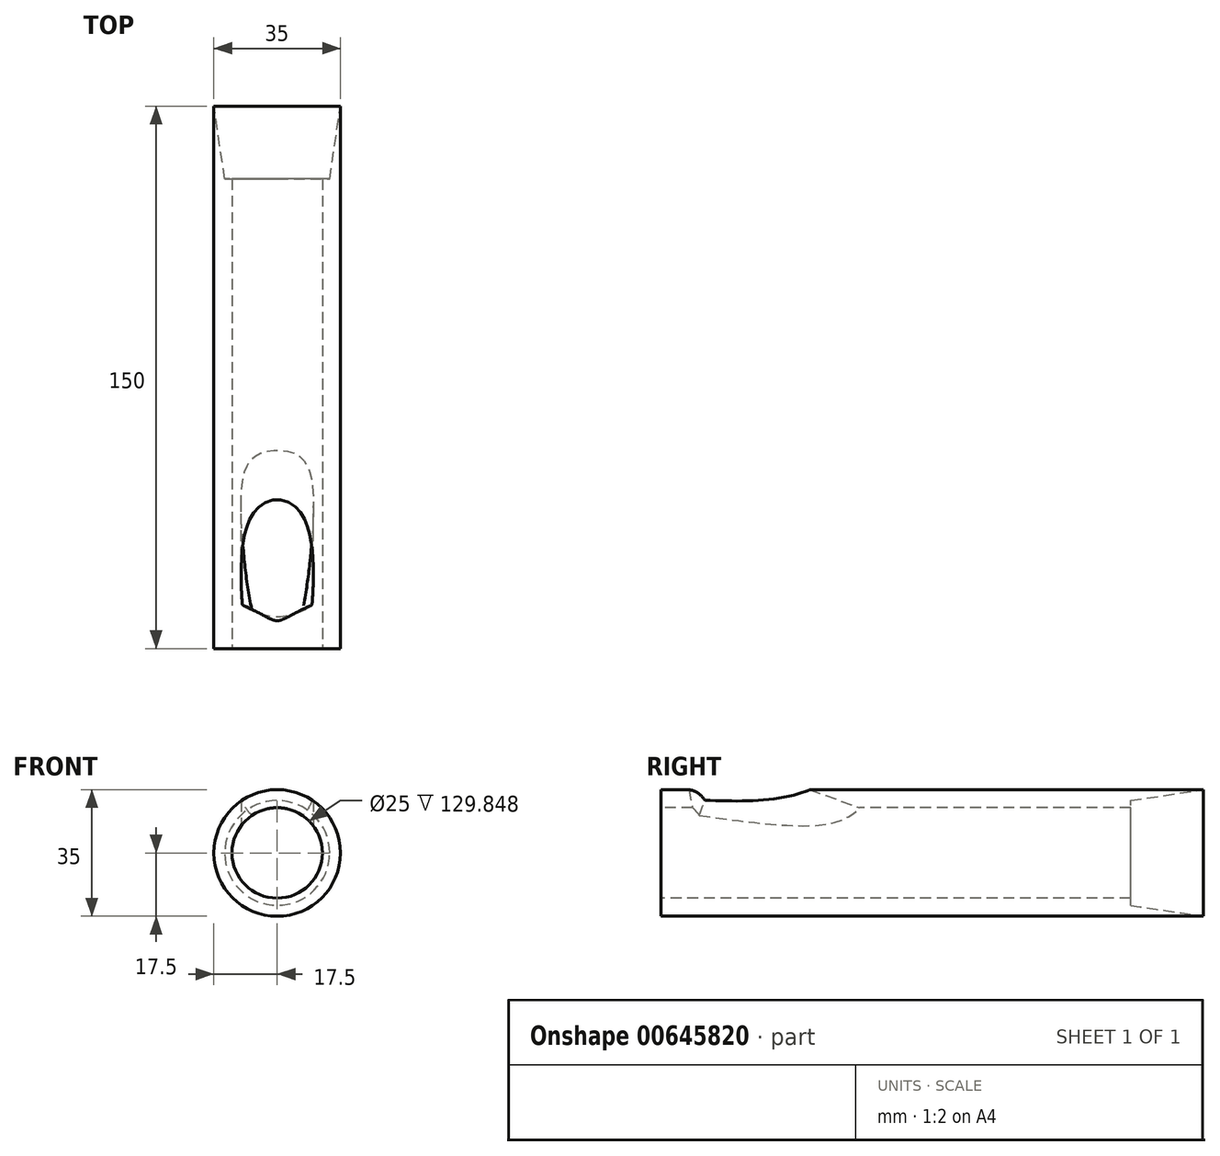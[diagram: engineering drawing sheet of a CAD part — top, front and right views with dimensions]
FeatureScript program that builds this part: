
annotation { "Feature Type Name" : "Feature", "Feature Type Description" : "" }
export const myFeature = defineFeature(function(context is Context, id is Id, definition is map)
    precondition{}
    {
        {
            var Q0;
            Q0=qCreatedBy(makeId("Top.planeOp"),FACE);
            var sketch = newSketch(context, id + "F0", { "sketchPlane" : qUnion([Q0])});
            skLineSegment(sketch, "E0", {"start": v(0, 0) * mm, "end": v(0, 150) * mm, "construction": true});
            skLineSegment(sketch, "E1", {"start": v(17.5, 0) * mm, "end": v(17.5, 150) * mm, "construction": true});
            skLineSegment(sketch, "E2", {"start": v(-61.8, 150) * mm, "end": v(89.31, 150) * mm, "construction": true});
            skLineSegment(sketch, "E3", {"start": v(12.5, 0) * mm, "end": v(12.5, 150) * mm, "construction": true});
            skLineSegment(sketch, "E4", {"start": v(-32.67, 60) * mm, "end": v(48.75, 60) * mm, "construction": true});
            skLineSegment(sketch, "E5", {"start": v(12.5, 0) * mm, "end": v(17.5, 0) * mm});
            skPoint(sketch, "E6", {"position": v(17.5, 60) * mm});
            skLineSegment(sketch, "E7", {"start": v(17.5, 0) * mm, "end": v(17.5, 60) * mm});
            skLineSegment(sketch, "E8", {"start": v(17.5, 150) * mm, "end": v(17.5, 60) * mm});
            skPoint(sketch, "E9", {"position": v(12.5, 129.85) * mm});
            skLineSegment(sketch, "E10", {"start": v(14.5, 129.85) * mm, "end": v(12.5, 129.85) * mm});
            skLineSegment(sketch, "E11", {"start": v(14.5, 129.85) * mm, "end": v(17.5, 150) * mm});
            skLineSegment(sketch, "E12", {"start": v(12.5, 0) * mm, "end": v(12.5, 129.85) * mm});
            skSolve(sketch);
        }
        {
            var Q0;
            Q0=makeQuery(id+"F0.imprint","IMPRINT",FACE,{"disambiguationData":[TD([[makeQuery(id+"F0.imprint","IMPRINT",EDGE,{"derivedFrom":sQuery(id+"F0.wireOp",EDGE,"E5")}),1.0]])]});
            var Q1;
            Q1=sQuery(id+"F0.wireOp",EDGE,"E0");
            revolve(context, id + "F1", {"entities" : qUnion([Q0]), "axis" : qUnion([Q1]), "revolveType" : RevolveType.FULL});
        }
        {
            var Q0;
            Q0=qCreatedBy(makeId("Top.planeOp"),FACE);
            var Q1;
            Q1=sQuery(id+"F0.wireOp",EDGE,"E4");
            cPlane(context, id + "F2", {"entities" : qUnion([Q0, Q1]), "cplaneType" : CPlaneType.LINE_ANGLE, "offset" : 17.5 * mm, "angle" : 70 * degree, "width" : 150 * mm, "height" : 150 * mm});
        }
        {
            var Q0;
            Q0=qCreatedBy(makeId("Front.planeOp"),FACE);
            cPlane(context, id + "F3", {"entities" : qUnion([Q0]), "cplaneType" : CPlaneType.OFFSET, "offset" : 80 * mm, "oppositeDirection" : true, "width" : 150 * mm, "height" : 150 * mm});
        }
        {
            var Q0;
            Q0=qCreatedBy(id+"F2.planeOp",FACE);
            var sketch = newSketch(context, id + "F4", { "sketchPlane" : qUnion([Q0])});
            skPoint(sketch, "E13", {"position": v(0, -32.9) * mm});
            skPoint(sketch, "E14", {"position": v(0, 20.52) * mm});
            skSolve(sketch);
        }
        {
            var Q0;
            Q0=sQuery(id+"F4.wireOp",VERTEX,"E14");
            var Q1;
            Q1=makeQuery(id+"F1.opRevolve","SWEPT_BODY",BODY,{"disambiguationData":[OSD([sQuery(id+"F0.wireOp",EDGE,"E5"),sQuery(id+"F0.wireOp",EDGE,"E7"),sQuery(id+"F0.wireOp",EDGE,"E8"),sQuery(id+"F0.wireOp",EDGE,"E10"),sQuery(id+"F0.wireOp",EDGE,"E11"),sQuery(id+"F0.wireOp",EDGE,"E12")])]});
            hole(context, id + "F5", {"style" : HoleStyle.SIMPLE, "endStyle" : HoleEndStyle.BLIND, "holeDiameter" : 20 * mm, "majorDiameter" : 5 * mm, "holeDepth" : 50 * mm, "isTappedThrough" : true, "tappedDepth" : 12 * mm, "tapClearance" : 3, "startFromSketch" : true, "locations" : qUnion([Q0]), "scope" : qUnion([Q1])});
        }
    });
